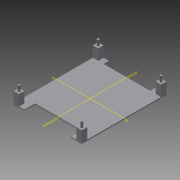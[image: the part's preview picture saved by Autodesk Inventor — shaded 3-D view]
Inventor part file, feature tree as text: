
AUTODESK INVENTOR PART (.ipt)
format: ipt  version: 2015 SP2 (Build 190223200, 223)  size: 150,016 bytes
history: native  units: in
note: dims shown in document units (in); Inventor stores cm internally (conversion verified against a paired STEP export)
features: extrude x4, mirror x4, sketch x4, plane x2, projected_geometry x2
ambient origin geometry x8: Origin, YZ Plane, XZ Plane, XY Plane, X Axis, Y Axis, Z Axis, Center Point
bodies: Solid3 (feature_tree)
feature tree (16):
  extrude  "Extrusion4"  Depth=2.1in
  extrude  "Extrusion5"  Depth=0.1181in
  plane  "Work Plane2"
  mirror  "Mirror2"
  plane  "Work Plane3"
  mirror  "Mirror3"
  extrude  "Extrusion8"  Depth=0.1181in
  mirror  "Mirror10"
  mirror  "Mirror11"
  extrude  "Extrusion9"  Depth=0.1969in
  sketch  "Sketch1"  dims[d0=2.7in d1=2.1in]
  sketch  "Sketch5"  dims[d2=0.1016in d3=0.1181in]
  sketch  "Sketch7"  dims[d4=0.3in d5=0.1181in]
  projected_geometry  "Projected Loop2"
  sketch  "Sketch8"  dims[d6=1.4in d8=0.1181in d9=0.5512in d10=0.0984in d26=0.0394in d27=0.0in d32=0.3937in d33=0.0in d46=0.1969in d47=-1.2469in d48=-1.5469in d49=0.1969in d50=0.1969in d53=0.1969in d54=0.0783in d62=0.1969in d63=0.0in d64=2.1in d65=1.7063in d66=0.1969in d67=0.0394in d68=0.0in d69=3.0937in d72=0.3937in d73=0.1969in d74=0.1969in]
  projected_geometry  "Projected Loop3"
